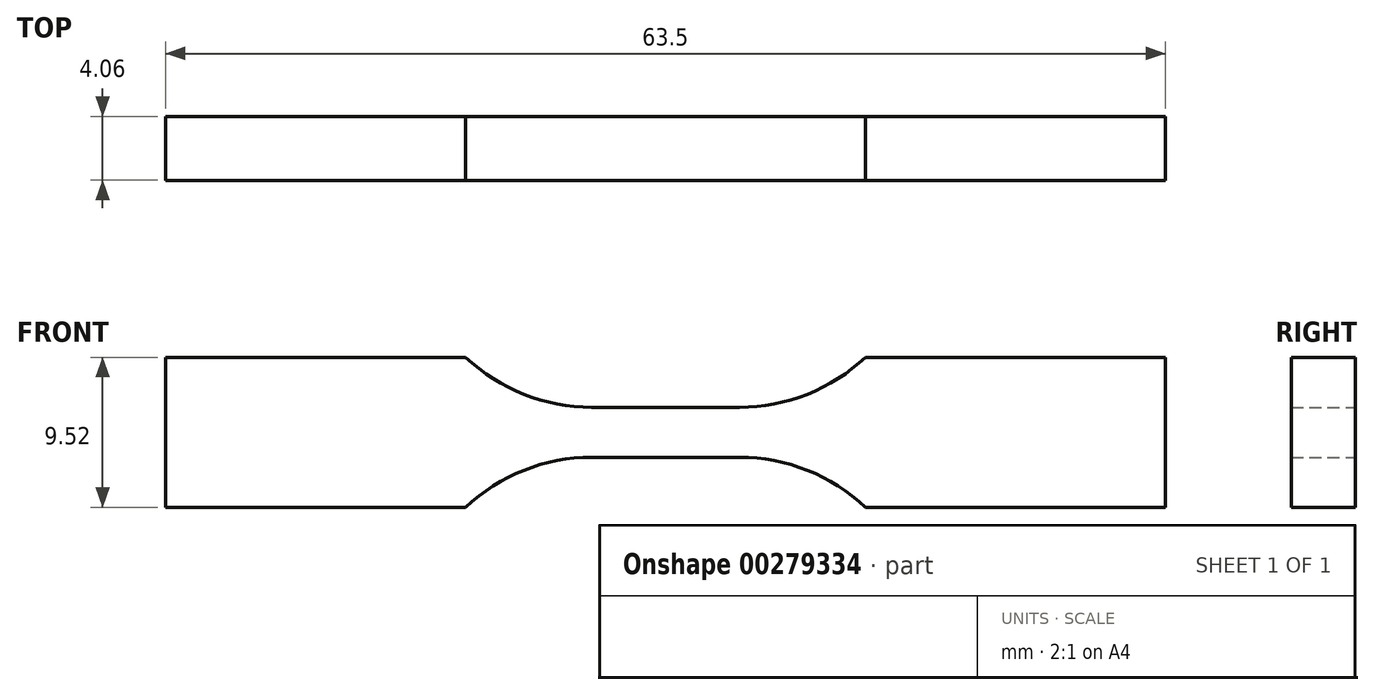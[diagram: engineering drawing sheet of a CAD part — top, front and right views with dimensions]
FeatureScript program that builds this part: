
annotation { "Feature Type Name" : "Feature", "Feature Type Description" : "" }
export const myFeature = defineFeature(function(context is Context, id is Id, definition is map)
    precondition{}
    {
        {
            var Q0;
            Q0=qCreatedBy(makeId("Front.planeOp"),FACE);
            var sketch = newSketch(context, id + "F0", { "sketchPlane" : qUnion([Q0])});
            skLineSegment(sketch, "E0", {"start": v(0, 1.59) * mm, "end": v(4.7, 1.59) * mm});
            skArc(sketch, "E1", {"start": v(4.7, 1.59) * mm, "mid": v(9, 2.41) * mm, "end": v(12.7, 4.76) * mm});
            skLineSegment(sketch, "E2", {"start": v(12.7, 4.76) * mm, "end": v(31.75, 4.76) * mm});
            skLineSegment(sketch, "E3.MirrorCS", {"start": v(12.7, -4.76) * mm, "end": v(31.75, -4.76) * mm});
            skLineSegment(sketch, "E4.MirrorCS", {"start": v(0, -1.59) * mm, "end": v(4.7, -1.59) * mm});
            skArc(sketch, "E5.MirrorCS", {"start": v(4.7, -1.59) * mm, "mid": v(9, -2.41) * mm, "end": v(12.7, -4.76) * mm});
            skArc(sketch, "E6.MirrorCS", {"start": v(-4.7, -1.59) * mm, "mid": v(-9, -2.41) * mm, "end": v(-12.7, -4.76) * mm});
            skLineSegment(sketch, "E7.MirrorCS", {"start": v(0, 1.59) * mm, "end": v(-4.7, 1.59) * mm});
            skArc(sketch, "E8.MirrorCS", {"start": v(-4.7, 1.59) * mm, "mid": v(-9, 2.41) * mm, "end": v(-12.7, 4.76) * mm});
            skLineSegment(sketch, "E9.MirrorCS", {"start": v(-12.7, -4.76) * mm, "end": v(-31.75, -4.76) * mm});
            skLineSegment(sketch, "E10.MirrorCS", {"start": v(0, -1.59) * mm, "end": v(-4.7, -1.59) * mm});
            skLineSegment(sketch, "E11.MirrorCS", {"start": v(-12.7, 4.76) * mm, "end": v(-31.75, 4.76) * mm});
            skLineSegment(sketch, "E12", {"start": v(-31.75, 4.76) * mm, "end": v(-31.75, -4.76) * mm});
            skLineSegment(sketch, "E13", {"start": v(31.75, 4.76) * mm, "end": v(31.75, -4.76) * mm});
            skSolve(sketch);
        }
        {
            var Q0;
            Q0=makeQuery(id+"F0.imprint","IMPRINT",FACE,{"disambiguationData":[TD([[makeQuery(id+"F0.imprint","IMPRINT",EDGE,{"derivedFrom":sQuery(id+"F0.wireOp",EDGE,"E0")}),-1.0]])]});
            extrude(context, id + "F1", {"entities" : qUnion([Q0]), "depth" : 4.06 * mm});
        }
    });
